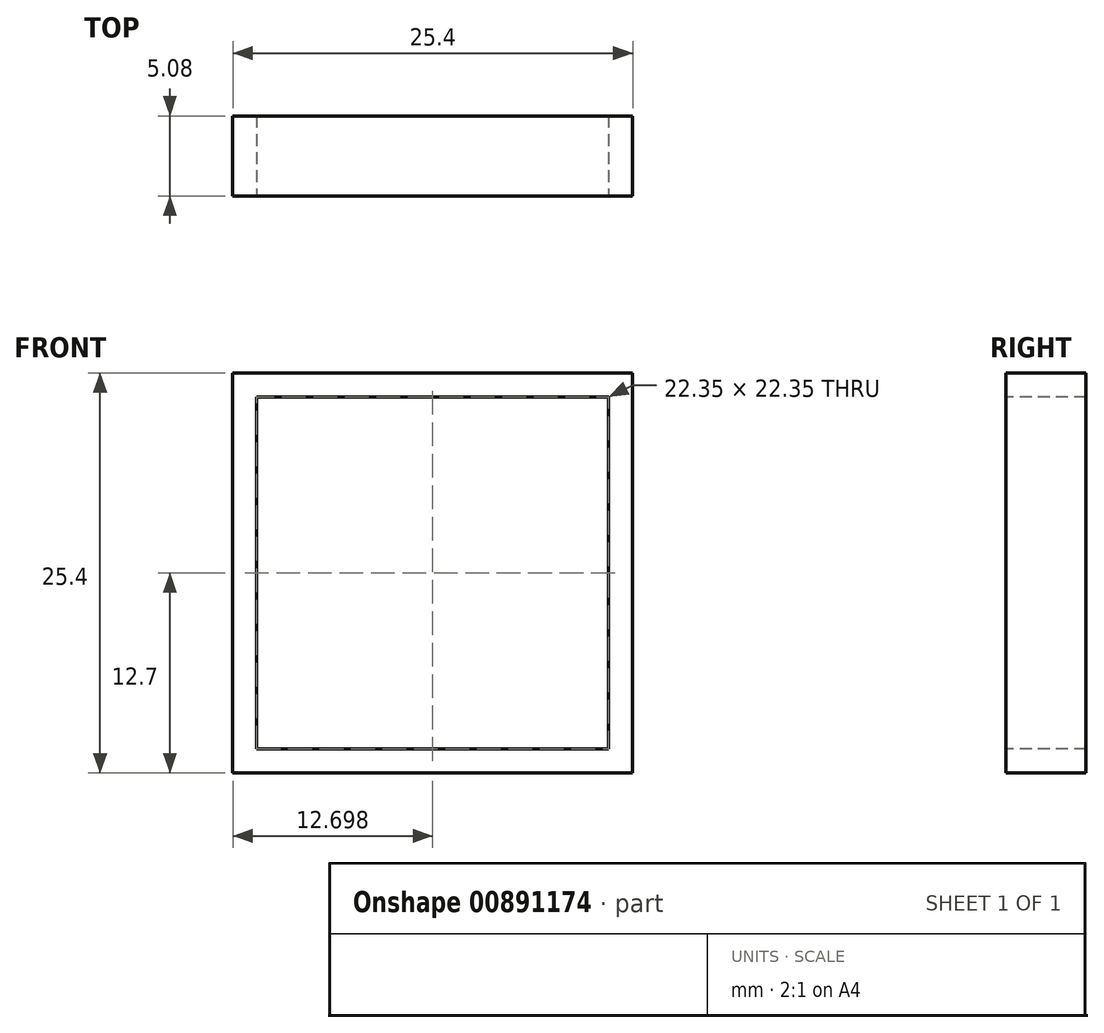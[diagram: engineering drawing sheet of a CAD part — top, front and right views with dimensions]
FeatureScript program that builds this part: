
annotation { "Feature Type Name" : "Feature", "Feature Type Description" : "" }
export const myFeature = defineFeature(function(context is Context, id is Id, definition is map)
    precondition{}
    {
        {
            var Q0;
            Q0=qCreatedBy(makeId("Front.planeOp"),FACE);
            var sketch = newSketch(context, id + "F0", { "sketchPlane" : qUnion([Q0])});
            skLineSegment(sketch, "E0.bottom", {"start": v(-26.3, -0.07) * mm, "end": v(-0.9, -0.07) * mm});
            skLineSegment(sketch, "E0.top", {"start": v(-26.3, -25.47) * mm, "end": v(-0.9, -25.47) * mm});
            skLineSegment(sketch, "E0.left", {"start": v(-26.3, -0.07) * mm, "end": v(-26.3, -25.47) * mm});
            skLineSegment(sketch, "E0.right", {"start": v(-0.9, -0.07) * mm, "end": v(-0.9, -25.47) * mm});
            skSolve(sketch);
        }
        {
            var Q0;
            Q0=makeQuery(id+"F0.imprint","IMPRINT",FACE,{"disambiguationData":[TD([[makeQuery(id+"F0.imprint","IMPRINT",EDGE,{"derivedFrom":sQuery(id+"F0.wireOp",EDGE,"E0.bottom")}),-1.0]])]});
            extrude(context, id + "F1", {"entities" : qUnion([Q0]), "depth" : 5.08 * mm, "offsetDistance" : 25.4 * mm});
        }
        {
            var Q0;
            Q0=makeQuery(id+"F1.opExtrude","CAP_FACE",FACE,{"disambiguationData":[OSD([sQuery(id+"F0.wireOp",EDGE,"E0.bottom"),sQuery(id+"F0.wireOp",EDGE,"E0.top"),sQuery(id+"F0.wireOp",EDGE,"E0.left"),sQuery(id+"F0.wireOp",EDGE,"E0.right")])],"isStart":false});
            var sketch = newSketch(context, id + "F2", { "sketchPlane" : qUnion([Q0])});
            skLineSegment(sketch, "E1.0", {"start": v(-24.78, -1.6) * mm, "end": v(-2.43, -1.6) * mm});
            skLineSegment(sketch, "E1.1", {"start": v(-24.78, -1.6) * mm, "end": v(-24.78, -23.95) * mm});
            skLineSegment(sketch, "E1.2", {"start": v(-24.78, -23.95) * mm, "end": v(-2.43, -23.95) * mm});
            skLineSegment(sketch, "E1.3", {"start": v(-2.43, -1.6) * mm, "end": v(-2.43, -23.95) * mm});
            skSolve(sketch);
        }
        {
            var Q0;
            Q0=makeQuery(id+"F2.imprint","IMPRINT",FACE,{"disambiguationData":[TD([[makeQuery(id+"F2.imprint","IMPRINT",EDGE,{"derivedFrom":sQuery(id+"F2.wireOp",EDGE,"E1.0")}),-1.0]])]});
            extrude(context, id + "F3", {"entities" : qUnion([Q0]), "operationType" : NewBodyOperationType.REMOVE, "oppositeDirection" : true, "depth" : 25.4 * mm, "offsetDistance" : 25.4 * mm, "hasSecondDirection" : true, "secondDirectionOppositeDirection" : false, "secondDirectionDepth" : 25.4 * mm});
        }
    });
